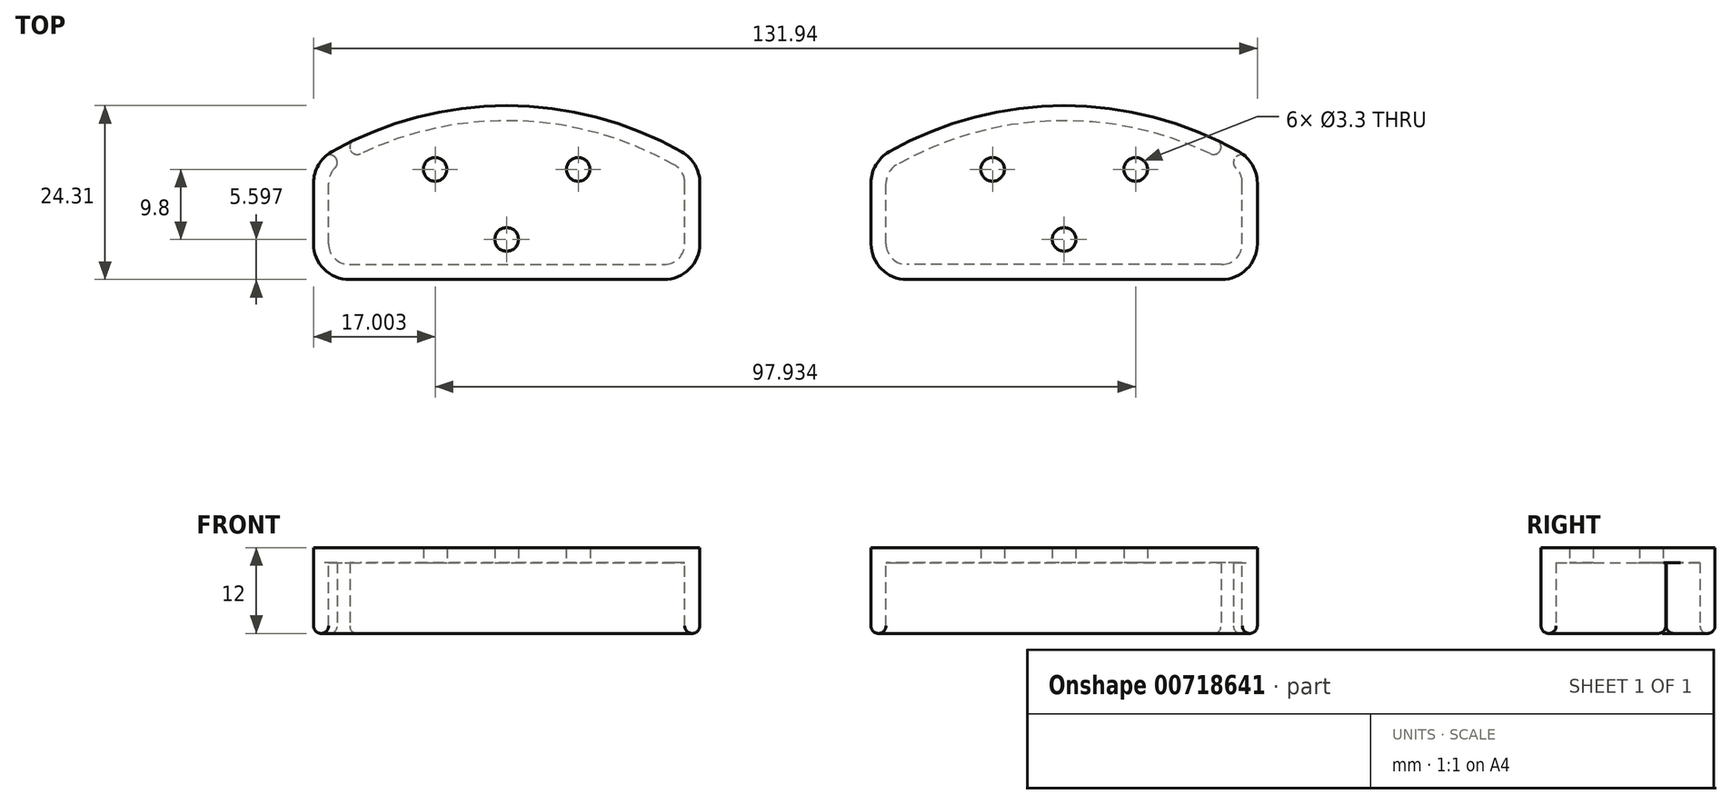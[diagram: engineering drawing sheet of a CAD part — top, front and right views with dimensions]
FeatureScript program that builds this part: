
annotation { "Feature Type Name" : "Feature", "Feature Type Description" : "" }
export const myFeature = defineFeature(function(context is Context, id is Id, definition is map)
    precondition{}
    {
        {
            var Q0;
            Q0=qCreatedBy(makeId("Top.planeOp"),FACE);
            var sketch = newSketch(context, id + "F0", { "sketchPlane" : qUnion([Q0])});
            skLineSegment(sketch, "E0.top", {"start": v(-21.47, -4.94) * mm, "end": v(22.53, -4.94) * mm});
            skPoint(sketch, "E1.visualSharp", {"position": v(-26.47, 11.36) * mm});
            skPoint(sketch, "E2.visualSharp", {"position": v(-26.47, -4.94) * mm});
            skArc(sketch, "E2.filletArc", {"start": v(-26.47, 0.06) * mm, "mid": v(-25, -3.48) * mm, "end": v(-21.47, -4.94) * mm});
            skPoint(sketch, "E3.visualSharp", {"position": v(27.53, -4.94) * mm});
            skArc(sketch, "E3.filletArc", {"start": v(22.53, -4.94) * mm, "mid": v(26.07, -3.48) * mm, "end": v(27.53, 0.06) * mm});
            skPoint(sketch, "E4.visualSharp", {"position": v(27.53, 11.36) * mm});
            skArc(sketch, "E5", {"start": v(25, 12.9) * mm, "mid": v(0.53, 19.37) * mm, "end": v(-23.94, 12.9) * mm});
            skArc(sketch, "E6.filletArc", {"start": v(-23.94, 12.9) * mm, "mid": v(-25.79, 11.07) * mm, "end": v(-26.47, 8.56) * mm});
            skArc(sketch, "E7.filletArc", {"start": v(27.53, 8.56) * mm, "mid": v(26.85, 11.07) * mm, "end": v(25, 12.9) * mm});
            skLineSegment(sketch, "E8", {"start": v(27.53, 0.06) * mm, "end": v(27.53, 8.56) * mm});
            skLineSegment(sketch, "E9", {"start": v(-26.47, 0.06) * mm, "end": v(-26.47, 8.56) * mm});
            skSolve(sketch);
        }
        {
            var Q0;
            Q0 = qSketchRegion(id + "F0", true);
            extrude(context, id + "F1", {"entities" : qUnion([Q0]), "depth" : 12 * mm, "offsetDistance" : 25 * mm});
        }
        {
            var Q0;
            Q0=makeQuery(id+"F1.opExtrude","CAP_FACE",FACE,{"disambiguationData":[OSD([sQuery(id+"F0.wireOp",EDGE,"E0.top"),sQuery(id+"F0.wireOp",EDGE,"6gFdXtkz-RAXD-tAZa-5YQp-rFPgbps3vCQl"),sQuery(id+"F0.wireOp",EDGE,"7FP5Ciz9-t9h5-owkY-3HIo-5qKGIlyv6VmH"),sQuery(id+"F0.wireOp",EDGE,"L5yFmjzV-bXwV-Ews7-FPJb-ulIHadGNXdZs")])],"isStart":true});
            shell(context, id + "F2", {"entities" : qUnion([Q0]), "thickness" : 2.1 * mm});
        }
        {
            var Q0;
            Q0=makeQuery(id+"F2.opShell","OFFSET_FACE",FACE,{"disambiguationData":[OSD([sQuery(id+"F0.wireOp",EDGE,"E0.top"),sQuery(id+"F0.wireOp",EDGE,"6gFdXtkz-RAXD-tAZa-5YQp-rFPgbps3vCQl"),sQuery(id+"F0.wireOp",EDGE,"7FP5Ciz9-t9h5-owkY-3HIo-5qKGIlyv6VmH"),sQuery(id+"F0.wireOp",EDGE,"L5yFmjzV-bXwV-Ews7-FPJb-ulIHadGNXdZs"),sQuery(id+"F0.wireOp",EDGE,"E1.filletArc"),sQuery(id+"F0.wireOp",EDGE,"E2.filletArc"),sQuery(id+"F0.wireOp",EDGE,"E3.filletArc"),sQuery(id+"F0.wireOp",EDGE,"E4.filletArc")])]});
            var sketch = newSketch(context, id + "F3", { "sketchPlane" : qUnion([Q0])});
            skCircle(sketch, "E10", {"center": v(10.53, -10.46) * mm, "radius": 1.65 * mm});
            skCircle(sketch, "E11", {"center": v(-9.47, -10.46) * mm, "radius": 1.65 * mm});
            skCircle(sketch, "E12", {"center": v(0.53, -0.66) * mm, "radius": 1.65 * mm});
            skPoint(sketch, "E13", {"position": v(0.53, -17.27) * mm});
            skSolve(sketch);
        }
        {
            var Q0;
            Q0 = qSketchRegion(id + "F3", true);
            extrude(context, id + "F4", {"entities" : qUnion([Q0]), "operationType" : NewBodyOperationType.REMOVE, "oppositeDirection" : true, "depth" : 5 * mm, "offsetDistance" : 25 * mm});
        }
        {
            var Q0;
            Q0=makeQuery(id+"F1.opExtrude","CAP_FACE",FACE,{"disambiguationData":[OSD([sQuery(id+"F0.wireOp",EDGE,"E0.top"),sQuery(id+"F0.wireOp",EDGE,"E2.filletArc"),sQuery(id+"F0.wireOp",EDGE,"E3.filletArc"),sQuery(id+"F0.wireOp",EDGE,"u3qg62mw-WA6E-kwH1-q1Hp-9531uLtv6cL0"),sQuery(id+"F0.wireOp",EDGE,"OSvv4fIa-EkMu-YqBA-zQEY-JU0DAZX49fD7"),sQuery(id+"F0.wireOp",EDGE,"E5"),sQuery(id+"F0.wireOp",EDGE,"E6.filletArc"),sQuery(id+"F0.wireOp",EDGE,"E7.filletArc")])],"isStart":true});
            fillet(context, id + "F5", {"entities" : qUnion([Q0]), "radius" : 1.05 * mm, "tangentPropagation" : true, "allowEdgeOverflow" : false});
        }
        {
            var Q0;
            Q0=makeQuery(id+"F2.opShell","OFFSET_FACE",FACE,{"disambiguationData":[OSD([sQuery(id+"F0.wireOp",EDGE,"E0.top"),sQuery(id+"F0.wireOp",EDGE,"E2.filletArc"),sQuery(id+"F0.wireOp",EDGE,"E3.filletArc"),sQuery(id+"F0.wireOp",EDGE,"E5"),sQuery(id+"F0.wireOp",EDGE,"E6.filletArc"),sQuery(id+"F0.wireOp",EDGE,"E7.filletArc"),sQuery(id+"F0.wireOp",EDGE,"E8"),sQuery(id+"F0.wireOp",EDGE,"E9")])]});
            var sketch = newSketch(context, id + "F6", { "sketchPlane" : qUnion([Q0])});
            skLineSegment(sketch, "E14", {"start": v(-22.82, -11.06) * mm, "end": v(-23.86, -13.06) * mm});
            skLineSegment(sketch, "E15", {"start": v(-23.86, -13.06) * mm, "end": v(-21.82, -14.12) * mm});
            skLineSegment(sketch, "E16", {"start": v(-21.82, -14.12) * mm, "end": v(-20.78, -12.13) * mm});
            skLineSegment(sketch, "E17", {"start": v(-20.78, -12.13) * mm, "end": v(-22.82, -11.06) * mm});
            skSolve(sketch);
        }
        {
            var Q0;
            Q0 = qSketchRegion(id + "F6", true);
            extrude(context, id + "F7", {"entities" : qUnion([Q0]), "operationType" : NewBodyOperationType.REMOVE, "depth" : 17 * mm, "offsetDistance" : 25 * mm});
        }
        {
            var Q0;
            Q0=makeQuery(id+"F7.boolean.opBoolean","INTERSECT",EDGE,{"derivedFrom":[makeQuery(id+"F5.opFillet","BLEND_FACE",FACE,{"disambiguationData":[OSD([sQuery(id+"F0.wireOp",EDGE,"E5")])]}),makeQuery(id+"F7.opExtrude","SWEPT_FACE",FACE,{"disambiguationData":[OSD([sQuery(id+"F6.wireOp",EDGE,"E14")])]})]});
            var Q1;
            Q1=makeQuery(id+"F7.boolean.opBoolean","INTERSECT",EDGE,{"derivedFrom":[makeQuery(id+"F5.opFillet","BLEND_FACE",FACE,{"disambiguationData":[OSD([sQuery(id+"F0.wireOp",EDGE,"E5")])]}),makeQuery(id+"F7.opExtrude","SWEPT_FACE",FACE,{"disambiguationData":[OSD([sQuery(id+"F6.wireOp",EDGE,"E16")])]})]});
            var Q2;
            Q2=makeQuery(id+"F7.boolean.opBoolean","INTERSECT",EDGE,{"derivedFrom":[makeQuery(id+"F2.opShell","OFFSET_FACE",FACE,{"disambiguationData":[OSD([sQuery(id+"F0.wireOp",EDGE,"E5")])]}),makeQuery(id+"F7.opExtrude","SWEPT_FACE",FACE,{"disambiguationData":[OSD([sQuery(id+"F6.wireOp",EDGE,"E16")])]})]});
            var Q3;
            Q3=makeQuery(id+"F7.boolean.opBoolean","INTERSECT",EDGE,{"derivedFrom":[makeQuery(id+"F1.opExtrude","SWEPT_FACE",FACE,{"disambiguationData":[OSD([sQuery(id+"F0.wireOp",EDGE,"E5")])]}),makeQuery(id+"F7.opExtrude","SWEPT_FACE",FACE,{"disambiguationData":[OSD([sQuery(id+"F6.wireOp",EDGE,"E16")])]})]});
            var Q4;
            Q4=makeQuery(id+"F7.boolean.opBoolean","INTERSECT",EDGE,{"derivedFrom":[makeQuery(id+"F1.opExtrude","SWEPT_FACE",FACE,{"disambiguationData":[OSD([sQuery(id+"F0.wireOp",EDGE,"E5")])]}),makeQuery(id+"F7.opExtrude","SWEPT_FACE",FACE,{"disambiguationData":[OSD([sQuery(id+"F6.wireOp",EDGE,"E14")])]})]});
            var Q5;
            Q5=makeQuery(id+"F7.boolean.opBoolean","INTERSECT",EDGE,{"derivedFrom":[makeQuery(id+"F2.opShell","OFFSET_FACE",FACE,{"disambiguationData":[OSD([sQuery(id+"F0.wireOp",EDGE,"E5")])]}),makeQuery(id+"F7.opExtrude","SWEPT_FACE",FACE,{"disambiguationData":[OSD([sQuery(id+"F6.wireOp",EDGE,"E14")])]})]});
            fillet(context, id + "F8", {"entities" : qUnion([Q0, Q1, Q2, Q3, Q4, Q5]), "radius" : 1.05 * mm, "tangentPropagation" : true, "allowEdgeOverflow" : false});
        }
        {
            var Q0;
            Q0=makeQuery(id+"F1.opExtrude","SWEPT_BODY",BODY,{"disambiguationData":[OSD([sQuery(id+"F0.wireOp",EDGE,"E0.top"),sQuery(id+"F0.wireOp",EDGE,"E2.filletArc"),sQuery(id+"F0.wireOp",EDGE,"E3.filletArc"),sQuery(id+"F0.wireOp",EDGE,"E5"),sQuery(id+"F0.wireOp",EDGE,"E6.filletArc"),sQuery(id+"F0.wireOp",EDGE,"E7.filletArc"),sQuery(id+"F0.wireOp",EDGE,"E8"),sQuery(id+"F0.wireOp",EDGE,"E9")])]});
            transform(context, id + "F9", {"entities" : qUnion([Q0]), "transformType" : TransformType.TRANSLATION_3D, "dx" : -39.5 * mm, "dy" : 0 * mm, "dz" : 0 * mm, "makeCopy" : false});
        }
        {
            var Q0;
            Q0=makeQuery(id+"F1.opExtrude","SWEPT_BODY",BODY,{"disambiguationData":[OSD([sQuery(id+"F0.wireOp",EDGE,"E0.top"),sQuery(id+"F0.wireOp",EDGE,"E2.filletArc"),sQuery(id+"F0.wireOp",EDGE,"E3.filletArc"),sQuery(id+"F0.wireOp",EDGE,"E5"),sQuery(id+"F0.wireOp",EDGE,"E6.filletArc"),sQuery(id+"F0.wireOp",EDGE,"E7.filletArc"),sQuery(id+"F0.wireOp",EDGE,"E8"),sQuery(id+"F0.wireOp",EDGE,"E9")])]});
            var Q1;
            Q1=qCreatedBy(makeId("Right.planeOp"),FACE);
            mirror(context, id + "F10", {"entities" : qUnion([Q0]), "mirrorPlane" : qUnion([Q1])});
        }
    });
